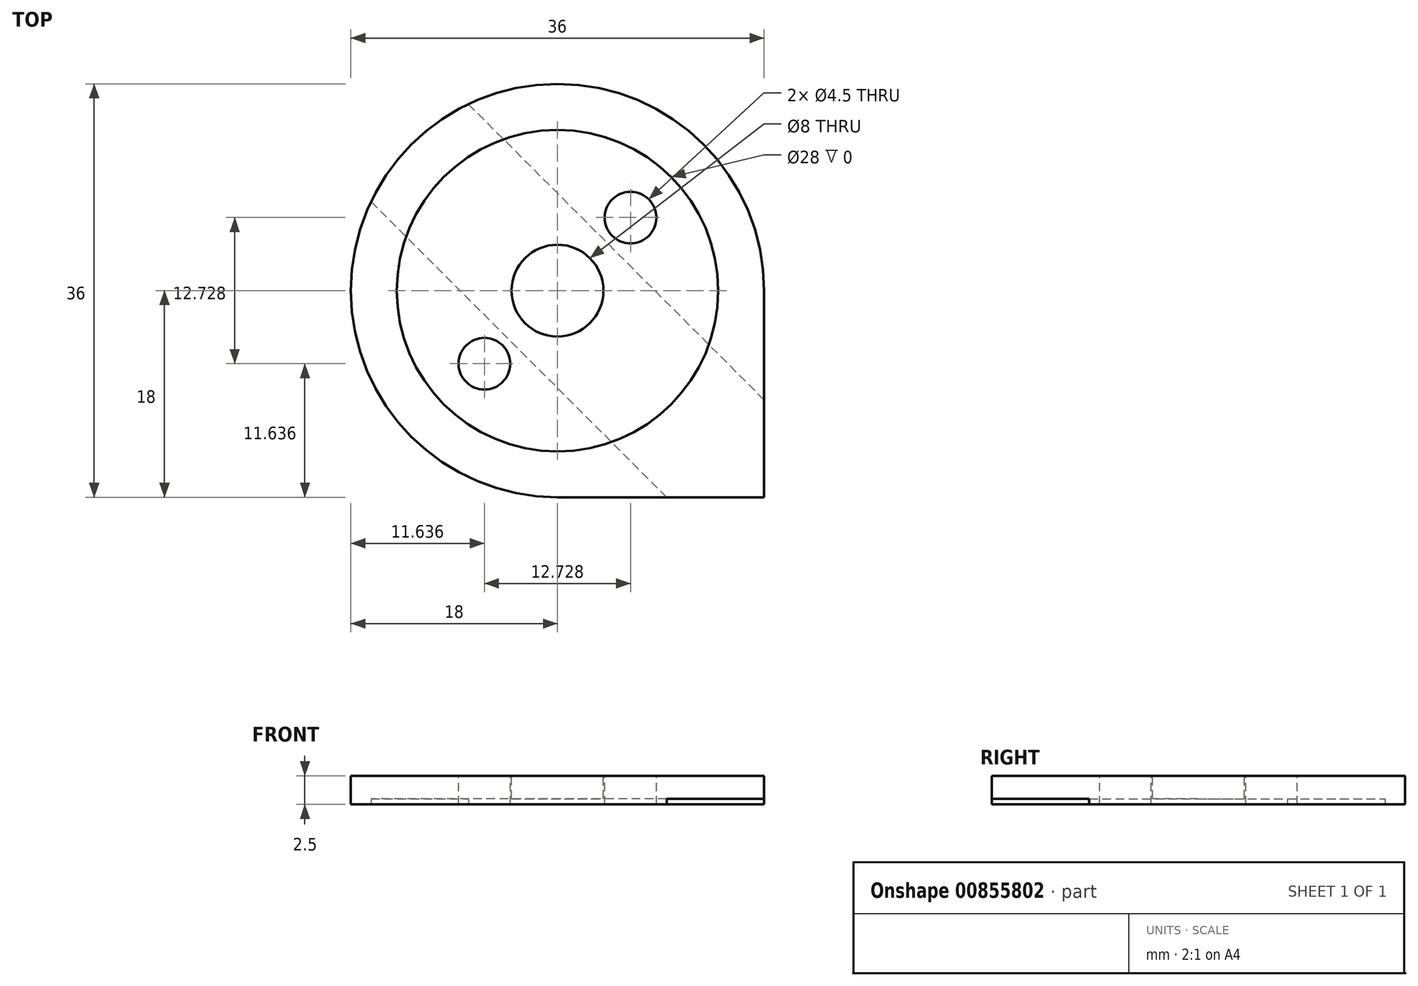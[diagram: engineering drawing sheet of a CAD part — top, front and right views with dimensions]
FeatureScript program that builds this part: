
annotation { "Feature Type Name" : "Feature", "Feature Type Description" : "" }
export const myFeature = defineFeature(function(context is Context, id is Id, definition is map)
    precondition{}
    {
        {
            var Q0;
            Q0=qCreatedBy(makeId("Top.planeOp"),FACE);
            var sketch = newSketch(context, id + "F0", { "sketchPlane" : qUnion([Q0])});
            skCircle(sketch, "E0", {"center": v(0, 0) * mm, "radius": 4 * mm});
            skLineSegment(sketch, "E1", {"start": v(0, 0) * mm, "end": v(0, 8) * mm});
            skCircle(sketch, "E2", {"center": v(6.36, 6.36) * mm, "radius": 2.25 * mm});
            skLineSegment(sketch, "E3", {"start": v(0, 0) * mm, "end": v(6.36, 6.36) * mm});
            skCircle(sketch, "E4.MirrorC", {"center": v(-6.36, -6.36) * mm, "radius": 2.25 * mm});
            skArc(sketch, "E5", {"start": v(0, 18) * mm, "mid": v(-12.73, 12.73) * mm, "end": v(-18, 0) * mm});
            skLineSegment(sketch, "E6", {"start": v(0, 0) * mm, "end": v(0, 0) * mm});
            skLineSegment(sketch, "E7", {"start": v(18, 0) * mm, "end": v(18, -18) * mm});
            skLineSegment(sketch, "E8", {"start": v(18, -18) * mm, "end": v(0, -18) * mm});
            skCircle(sketch, "E9", {"center": v(0, 0) * mm, "radius": 14 * mm});
            skLineSegment(sketch, "E10", {"start": v(0, 0) * mm, "end": v(18, 0) * mm});
            skLineSegment(sketch, "E11", {"start": v(-6.36, -6.36) * mm, "end": v(0, 0) * mm});
            skArc(sketch, "E12", {"start": v(-18, 0) * mm, "mid": v(-12.73, -12.73) * mm, "end": v(0, -18) * mm});
            skArc(sketch, "E13", {"start": v(18, 0) * mm, "mid": v(12.73, 12.73) * mm, "end": v(0, 18) * mm});
            skSolve(sketch);
        }
        {
            var Q0;
            {var subQ12=sQuery(id+"F0.wireOp",EDGE,"5gUyvu4n-H8Yu-rZ5o-7L1h-m2GLPaqCX34R");Q0=makeQuery(id+"F0.imprint","IMPRINT",FACE,{"disambiguationData":[TD([[makeQuery(id+"F0.imprint","IMPRINT",EDGE,{"derivedFrom":subQ12}),-1.0]])]});}
            var Q1;
            {var subQ10=sQuery(id+"F0.wireOp",EDGE,"E5");Q1=makeQuery(id+"F0.imprint","IMPRINT",FACE,{"disambiguationData":[TD([[makeQuery(id+"F0.imprint","IMPRINT",EDGE,{"derivedFrom":subQ10}),1.0]])]});}
            var Q2;
            {var subQ4=sQuery(id+"F0.wireOp",EDGE,"pYiCtXtq-HJty-5pja-FRCl-Y2SLxosvPTdB");Q2=makeQuery(id+"F0.imprint","IMPRINT",FACE,{"disambiguationData":[TD([[makeQuery(id+"F0.imprint","IMPRINT",EDGE,{"derivedFrom":subQ4}),-1.0]])]});}
            var Q3;
            {var subQ6=sQuery(id+"F0.wireOp",EDGE,"E7");Q3=makeQuery(id+"F0.imprint","IMPRINT",FACE,{"disambiguationData":[TD([[makeQuery(id+"F0.imprint","IMPRINT",EDGE,{"derivedFrom":subQ6}),-1.0]])]});}
            extrude(context, id + "F1", {"entities" : qUnion([Q0, Q1, Q2, Q3]), "depth" : 0 * mm, "offsetDistance" : 25 * mm});
        }
        {
            var Q0;
            Q0=qSketchRegion(id+"F0",true);
            var Q1;
            {var subQ0=sQuery(id+"F0.wireOp",EDGE,"E10");var subQ5=sQuery(id+"F0.wireOp",EDGE,"E0");var subQ13=makeQuery(id+"F0.imprint","INTERSECT",VERTEX,{"derivedFrom":[subQ5,subQ0]});Q1=makeQuery(id+"F0.imprint","IMPRINT",FACE,{"disambiguationData":[TD([[makeQuery(id+"F0.imprint","IMPRINT",EDGE,{"disambiguationData":[TD([[subQ13,1.0]])],"derivedFrom":subQ5}),-1.0]])]});}
            var Q2;
            {var subQ0=sQuery(id+"F0.wireOp",EDGE,"9Jcqm4WY-S0i0-zeqv-JkX0-I8y0cwtzbrRk");var subQ8=sQuery(id+"F0.wireOp",EDGE,"E0");var subQ13=makeQuery(id+"F0.imprint","INTERSECT",VERTEX,{"derivedFrom":[subQ8,subQ0]});Q2=makeQuery(id+"F0.imprint","IMPRINT",FACE,{"disambiguationData":[TD([[makeQuery(id+"F0.imprint","IMPRINT",EDGE,{"disambiguationData":[TD([[subQ13,1.0]])],"derivedFrom":subQ8}),-1.0]])]});}
            var Q3;
            {var subQ0=sQuery(id+"F0.wireOp",EDGE,"9Jcqm4WY-S0i0-zeqv-JkX0-I8y0cwtzbrRk");var subQ11=sQuery(id+"F0.wireOp",EDGE,"E0");var subQ12=makeQuery(id+"F0.imprint","INTERSECT",VERTEX,{"derivedFrom":[subQ11,subQ0]});Q3=makeQuery(id+"F0.imprint","IMPRINT",FACE,{"disambiguationData":[TD([[makeQuery(id+"F0.imprint","IMPRINT",EDGE,{"disambiguationData":[TD([[subQ12,-1.0]])],"derivedFrom":subQ11}),-1.0]])]});}
            var Q4;
            {var subQ0=sQuery(id+"F0.wireOp",EDGE,"VnMWNyeu-xD8e-0Uzf-ypBL-w7x0ykIT27B9");var subQ8=sQuery(id+"F0.wireOp",EDGE,"E0");var subQ13=makeQuery(id+"F0.imprint","INTERSECT",VERTEX,{"derivedFrom":[subQ8,subQ0]});Q4=makeQuery(id+"F0.imprint","IMPRINT",FACE,{"disambiguationData":[TD([[makeQuery(id+"F0.imprint","IMPRINT",EDGE,{"disambiguationData":[TD([[subQ13,-1.0]])],"derivedFrom":subQ8}),-1.0]])]});}
            var Q5;
            {var subQ0=sQuery(id+"F0.wireOp",EDGE,"E10");var subQ1=sQuery(id+"F0.wireOp",EDGE,"E0");var subQ2=makeQuery(id+"F0.imprint","INTERSECT",VERTEX,{"derivedFrom":[subQ1,subQ0]});Q5=makeQuery(id+"F0.imprint","IMPRINT",FACE,{"disambiguationData":[TD([[makeQuery(id+"F0.imprint","IMPRINT",EDGE,{"disambiguationData":[TD([[subQ2,1.0]])],"derivedFrom":subQ1}),1.0]])]});}
            var Q6;
            {var subQ0=sQuery(id+"F0.wireOp",EDGE,"E3");var subQ1=sQuery(id+"F0.wireOp",EDGE,"E0");var subQ2=makeQuery(id+"F0.imprint","INTERSECT",VERTEX,{"derivedFrom":[subQ1,subQ0]});Q6=makeQuery(id+"F0.imprint","IMPRINT",FACE,{"disambiguationData":[TD([[makeQuery(id+"F0.imprint","IMPRINT",EDGE,{"disambiguationData":[TD([[subQ2,-1.0]])],"derivedFrom":subQ1}),1.0]])]});}
            var Q7;
            {var subQ0=sQuery(id+"F0.wireOp",EDGE,"E1");var subQ1=sQuery(id+"F0.wireOp",EDGE,"E0");var subQ2=makeQuery(id+"F0.imprint","INTERSECT",VERTEX,{"derivedFrom":[subQ1,subQ0]});Q7=makeQuery(id+"F0.imprint","IMPRINT",FACE,{"disambiguationData":[TD([[makeQuery(id+"F0.imprint","IMPRINT",EDGE,{"disambiguationData":[TD([[subQ2,-1.0]])],"derivedFrom":subQ1}),1.0]])]});}
            var Q8;
            {var subQ0=sQuery(id+"F0.wireOp",EDGE,"E3");var subQ1=sQuery(id+"F0.wireOp",EDGE,"E0");var subQ2=makeQuery(id+"F0.imprint","INTERSECT",VERTEX,{"derivedFrom":[subQ1,subQ0]});Q8=makeQuery(id+"F0.imprint","IMPRINT",FACE,{"disambiguationData":[TD([[makeQuery(id+"F0.imprint","IMPRINT",EDGE,{"disambiguationData":[TD([[subQ2,1.0]])],"derivedFrom":subQ1}),1.0]])]});}
            extrude(context, id + "F2", {"entities" : qUnion([Q0, Q1, Q2, Q3, Q4, Q5, Q6, Q7, Q8]), "operationType" : NewBodyOperationType.ADD, "oppositeDirection" : true, "depth" : 2.5 * mm, "offsetDistance" : 25 * mm});
        }
        {
            var Q0;
            {var subQ0=sQuery(id+"F0.wireOp",EDGE,"E10");var subQ1=sQuery(id+"F0.wireOp",EDGE,"E0");var subQ2=makeQuery(id+"F0.imprint","INTERSECT",VERTEX,{"derivedFrom":[subQ1,subQ0]});Q0=makeQuery(id+"F0.imprint","IMPRINT",FACE,{"disambiguationData":[TD([[makeQuery(id+"F0.imprint","IMPRINT",EDGE,{"disambiguationData":[TD([[subQ2,1.0]])],"derivedFrom":subQ1}),1.0]])]});}
            var Q1;
            {var subQ0=sQuery(id+"F0.wireOp",EDGE,"E3");var subQ1=sQuery(id+"F0.wireOp",EDGE,"E0");var subQ2=makeQuery(id+"F0.imprint","INTERSECT",VERTEX,{"derivedFrom":[subQ1,subQ0]});Q1=makeQuery(id+"F0.imprint","IMPRINT",FACE,{"disambiguationData":[TD([[makeQuery(id+"F0.imprint","IMPRINT",EDGE,{"disambiguationData":[TD([[subQ2,1.0]])],"derivedFrom":subQ1}),1.0]])]});}
            var Q2;
            {var subQ0=sQuery(id+"F0.wireOp",EDGE,"E3");var subQ1=sQuery(id+"F0.wireOp",EDGE,"E0");var subQ2=makeQuery(id+"F0.imprint","INTERSECT",VERTEX,{"derivedFrom":[subQ1,subQ0]});Q2=makeQuery(id+"F0.imprint","IMPRINT",FACE,{"disambiguationData":[TD([[makeQuery(id+"F0.imprint","IMPRINT",EDGE,{"disambiguationData":[TD([[subQ2,-1.0]])],"derivedFrom":subQ1}),1.0]])]});}
            var Q3;
            {var subQ0=sQuery(id+"F0.wireOp",EDGE,"E1");var subQ1=sQuery(id+"F0.wireOp",EDGE,"E0");var subQ2=makeQuery(id+"F0.imprint","INTERSECT",VERTEX,{"derivedFrom":[subQ1,subQ0]});Q3=makeQuery(id+"F0.imprint","IMPRINT",FACE,{"disambiguationData":[TD([[makeQuery(id+"F0.imprint","IMPRINT",EDGE,{"disambiguationData":[TD([[subQ2,-1.0]])],"derivedFrom":subQ1}),1.0]])]});}
            extrude(context, id + "F3", {"entities" : qUnion([Q0, Q1, Q2, Q3]), "operationType" : NewBodyOperationType.REMOVE, "oppositeDirection" : true, "depth" : 3 * mm, "offsetDistance" : 25 * mm});
        }
        {
            var Q0;
            Q0=makeQuery(id+"F2.opExtrude","CAP_FACE",FACE,{"disambiguationData":[OSD([sQuery(id+"F0.wireOp",EDGE,"E2"),sQuery(id+"F0.wireOp",EDGE,"E4.MirrorC"),sQuery(id+"F0.wireOp",EDGE,"E5"),sQuery(id+"F0.wireOp",EDGE,"5gUyvu4n-H8Yu-rZ5o-7L1h-m2GLPaqCX34R"),sQuery(id+"F0.wireOp",EDGE,"1Qr6Kwjt-veDL-C7E2-Esiv-kxE1Q1Ce19U3"),sQuery(id+"F0.wireOp",EDGE,"pYiCtXtq-HJty-5pja-FRCl-Y2SLxosvPTdB"),sQuery(id+"F0.wireOp",EDGE,"jzTP4OU7-n7uz-U0up-Kohm-FM5JfBalmunU"),sQuery(id+"F0.wireOp",EDGE,"E7"),sQuery(id+"F0.wireOp",EDGE,"E8")])],"isStart":false});
            var sketch = newSketch(context, id + "F4", { "sketchPlane" : qUnion([Q0])});
            skLineSegment(sketch, "E14", {"start": v(0, 0) * mm, "end": v(-4.24, 4.24) * mm});
            skLineSegment(sketch, "E15", {"start": v(0, 0) * mm, "end": v(4.24, -4.24) * mm});
            skLineSegment(sketch, "E16", {"start": v(4.24, -4.24) * mm, "end": v(18, 9.51) * mm});
            skLineSegment(sketch, "E17", {"start": v(-4.24, 4.24) * mm, "end": v(9.51, 18) * mm});
            skLineSegment(sketch, "E18", {"start": v(-4.24, 4.24) * mm, "end": v(-16.97, -8.49) * mm});
            skLineSegment(sketch, "E19", {"start": v(4.24, -4.24) * mm, "end": v(-8.49, -16.97) * mm});
            skLineSegment(sketch, "E20", {"start": v(-16.97, -8.49) * mm, "end": v(-8.49, -16.97) * mm});
            skLineSegment(sketch, "E21", {"start": v(18, 0) * mm, "end": v(0, 0) * mm});
            skSolve(sketch);
        }
        {
            var Q0;
            Q0=qSketchRegion(id+"F4",true);
            var Q1;
            {var subQ2=sQuery(id+"F4.wireOp",EDGE,"E14");Q1=makeQuery(id+"F4.imprint","IMPRINT",FACE,{"disambiguationData":[TD([[makeQuery(id+"F4.imprint","IMPRINT",EDGE,{"derivedFrom":subQ2}),-1.0]])]});}
            var Q2;
            {var subQ11=sQuery(id+"F4.wireOp",EDGE,"E17");Q2=makeQuery(id+"F4.imprint","IMPRINT",FACE,{"disambiguationData":[TD([[makeQuery(id+"F4.imprint","IMPRINT",EDGE,{"derivedFrom":subQ11}),-1.0]])]});}
            extrude(context, id + "F5", {"entities" : qUnion([Q0, Q1, Q2]), "operationType" : NewBodyOperationType.REMOVE, "oppositeDirection" : true, "depth" : 0.5 * mm, "offsetDistance" : 25 * mm});
        }
    });
